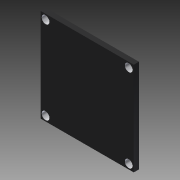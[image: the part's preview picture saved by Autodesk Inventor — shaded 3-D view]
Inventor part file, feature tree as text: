
AUTODESK INVENTOR PART (.ipt)
format: ipt  version: 2015 (Build 190159000, 159)  size: 185,856 bytes
history: native  units: mm
features: extrude x2, sketch x1
ambient origin geometry x8: Origin, YZ Plane, XZ Plane, XY Plane, X Axis, Y Axis, Z Axis, Center Point
bodies: Solid1 (feature_tree)
feature tree (3):
  sketch  "Sketch1"  dims[d2=3.0mm d3=3.0mm d4=2.0mm d5=0.0mm d6=2.2mm d7=0.0mm]
  extrude  "Extrusion1"  Depth=2.0mm TaperAngle=0.0deg
  extrude  "Extrusion2"  Depth=2.2mm TaperAngle=0.0deg
